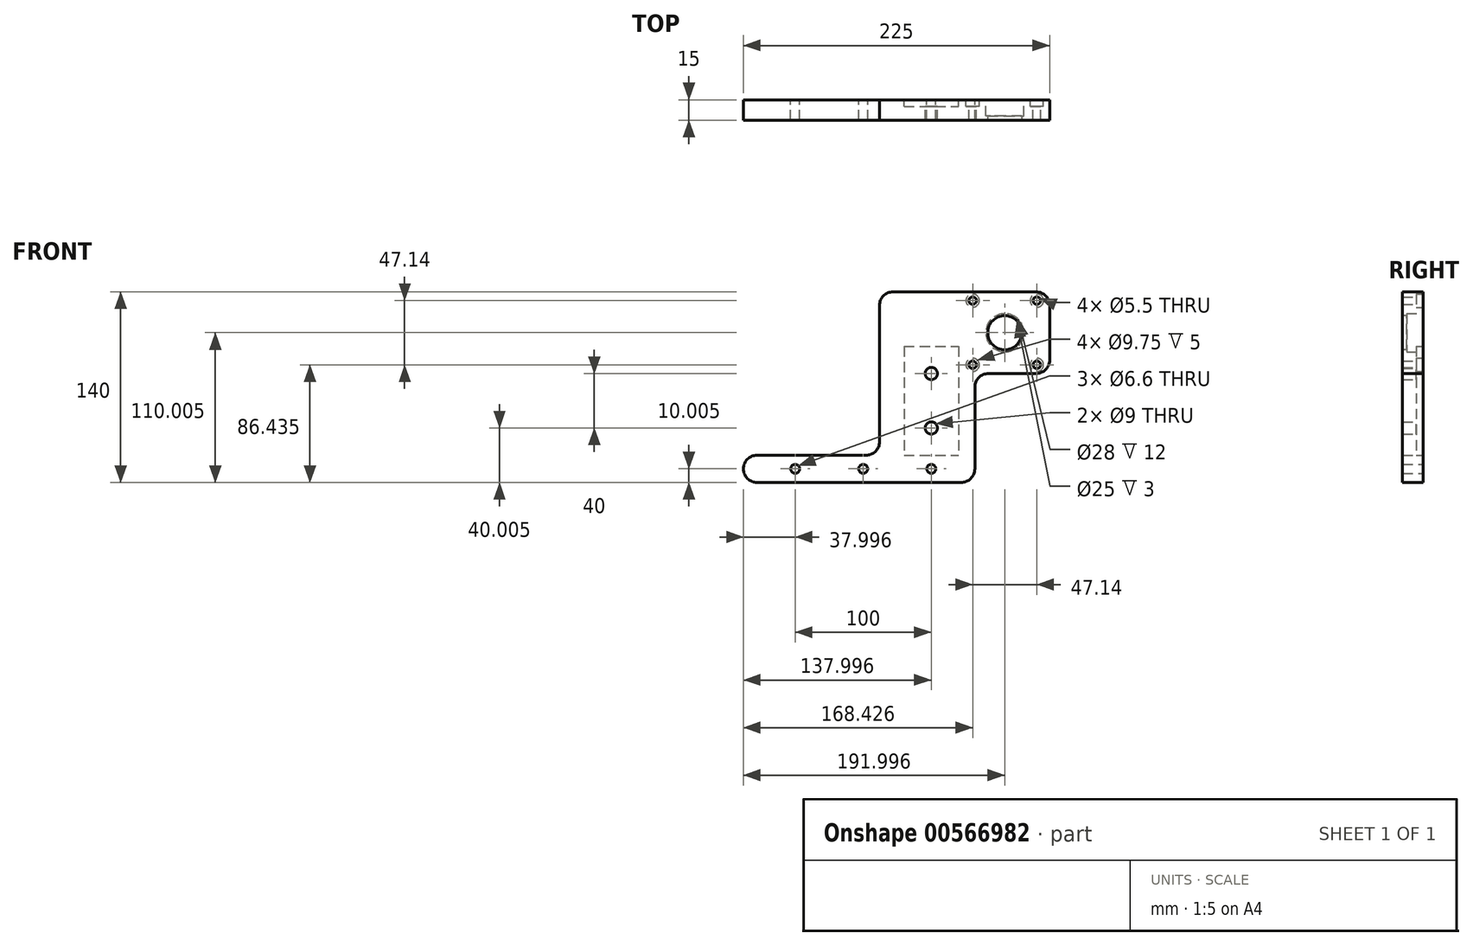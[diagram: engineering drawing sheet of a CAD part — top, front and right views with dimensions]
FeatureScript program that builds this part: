
annotation { "Feature Type Name" : "Feature", "Feature Type Description" : "" }
export const myFeature = defineFeature(function(context is Context, id is Id, definition is map)
    precondition{}
    {
        {
            var Q0;
            Q0=qCreatedBy(makeId("Front.planeOp"),FACE);
            var sketch = newSketch(context, id + "F0", { "sketchPlane" : qUnion([Q0])});
            skLineSegment(sketch, "E0", {"start": v(-57.93, 20.91) * mm, "end": v(62.07, 20.91) * mm});
            skLineSegment(sketch, "E1", {"start": v(62.07, 20.91) * mm, "end": v(62.07, -99.09) * mm});
            skLineSegment(sketch, "E2", {"start": v(62.07, -99.09) * mm, "end": v(162.07, -99.09) * mm});
            skLineSegment(sketch, "E3", {"start": v(162.07, -99.09) * mm, "end": v(162.07, -119.09) * mm});
            skLineSegment(sketch, "E4", {"start": v(162.07, -119.09) * mm, "end": v(-7.93, -119.09) * mm});
            skLineSegment(sketch, "E5", {"start": v(-7.93, -119.09) * mm, "end": v(-7.93, -39.09) * mm});
            skLineSegment(sketch, "E6", {"start": v(-7.93, -39.09) * mm, "end": v(-57.93, -39.09) * mm});
            skLineSegment(sketch, "E7", {"start": v(52.07, 10.91) * mm, "end": v(-47.93, 10.91) * mm, "construction": true});
            skLineSegment(sketch, "E8", {"start": v(-47.93, 10.91) * mm, "end": v(-47.93, -29.09) * mm, "construction": true});
            skLineSegment(sketch, "E9", {"start": v(-47.93, -29.09) * mm, "end": v(4.07, -29.09) * mm, "construction": true});
            skLineSegment(sketch, "E10", {"start": v(4.07, -29.09) * mm, "end": v(4.07, -119.09) * mm, "construction": true});
            skLineSegment(sketch, "E11", {"start": v(4.07, -119.09) * mm, "end": v(162.07, -119.09) * mm, "construction": true});
            skLineSegment(sketch, "E12", {"start": v(162.07, -119.09) * mm, "end": v(162.07, -99.09) * mm, "construction": true});
            skLineSegment(sketch, "E13", {"start": v(162.07, -99.09) * mm, "end": v(52.07, -99.09) * mm, "construction": true});
            skLineSegment(sketch, "E14", {"start": v(52.07, -99.09) * mm, "end": v(52.07, 10.91) * mm, "construction": true});
            skPoint(sketch, "E15", {"position": v(24.07, -109.09) * mm});
            skPoint(sketch, "E16", {"position": v(24.07, -79.09) * mm});
            skPoint(sketch, "E17", {"position": v(24.07, -39.09) * mm});
            skPoint(sketch, "E18", {"position": v(74.07, -109.09) * mm});
            skPoint(sketch, "E19", {"position": v(124.07, -109.09) * mm});
            skPoint(sketch, "E20", {"position": v(-29.93, -9.09) * mm});
            skPoint(sketch, "E21", {"position": v(-53.5, 14.48) * mm});
            skLineSegment(sketch, "E22", {"start": v(-44.33, -9.09) * mm, "end": v(-15.97, -9.09) * mm, "construction": true});
            skLineSegment(sketch, "E23", {"start": v(-29.93, 7.3) * mm, "end": v(-29.93, -21.44) * mm, "construction": true});
            skPoint(sketch, "E24.MirrorP", {"position": v(-53.5, -32.66) * mm});
            skPoint(sketch, "E25.MirrorP", {"position": v(-6.36, 14.48) * mm});
            skPoint(sketch, "E26.MirrorP", {"position": v(-6.36, -32.66) * mm});
            skLineSegment(sketch, "E27", {"start": v(-57.93, 20.91) * mm, "end": v(-62.93, 20.91) * mm});
            skLineSegment(sketch, "E28", {"start": v(-62.93, 20.91) * mm, "end": v(-62.93, -39.09) * mm});
            skLineSegment(sketch, "E29", {"start": v(-62.93, -39.09) * mm, "end": v(-57.93, -39.09) * mm});
            skSolve(sketch);
        }
        {
            var Q0;
            Q0=makeQuery(id+"F0.imprint","IMPRINT",FACE,{"disambiguationData":[TD([[makeQuery(id+"F0.imprint","IMPRINT",EDGE,{"derivedFrom":sQuery(id+"F0.wireOp",EDGE,"E0")}),-1.0]])]});
            extrude(context, id + "F1", {"entities" : qUnion([Q0]), "depth" : 15 * mm});
        }
        {
            var Q0;
            Q0=sQuery(id+"F0.wireOp",VERTEX,"E16");
            var Q1;
            Q1=sQuery(id+"F0.wireOp",VERTEX,"E17");
            var Q2;
            Q2=makeQuery(id+"F1.opExtrude","SWEPT_BODY",BODY,{"disambiguationData":[OSD([sQuery(id+"F0.wireOp",EDGE,"E0"),sQuery(id+"F0.wireOp",EDGE,"E1"),sQuery(id+"F0.wireOp",EDGE,"E2"),sQuery(id+"F0.wireOp",EDGE,"E3"),sQuery(id+"F0.wireOp",EDGE,"E4"),sQuery(id+"F0.wireOp",EDGE,"E5"),sQuery(id+"F0.wireOp",EDGE,"E6"),sQuery(id+"F0.wireOp",EDGE,"cvZF5QLb-uWAo-robz-iAHo-1Gj3ORty2Von")])]});
            hole(context, id + "F2", {"style" : HoleStyle.SIMPLE, "endStyle" : HoleEndStyle.THROUGH, "oppositeDirection" : true, "holeDiameter" : 9 * mm, "locations" : qUnion([Q0, Q1]), "scope" : qUnion([Q2]), "tappedDepth" : 12 * mm, "tapClearance" : 3});
        }
        {
            var Q0;
            Q0=sQuery(id+"F0.wireOp",VERTEX,"E15");
            var Q1;
            Q1=sQuery(id+"F0.wireOp",VERTEX,"E18");
            var Q2;
            Q2=sQuery(id+"F0.wireOp",VERTEX,"E19");
            var Q3;
            Q3=makeQuery(id+"F1.opExtrude","SWEPT_BODY",BODY,{"disambiguationData":[OSD([sQuery(id+"F0.wireOp",EDGE,"E0"),sQuery(id+"F0.wireOp",EDGE,"E1"),sQuery(id+"F0.wireOp",EDGE,"E2"),sQuery(id+"F0.wireOp",EDGE,"E3"),sQuery(id+"F0.wireOp",EDGE,"E4"),sQuery(id+"F0.wireOp",EDGE,"E5"),sQuery(id+"F0.wireOp",EDGE,"E6"),sQuery(id+"F0.wireOp",EDGE,"cvZF5QLb-uWAo-robz-iAHo-1Gj3ORty2Von")])]});
            hole(context, id + "F3", {"style" : HoleStyle.SIMPLE, "endStyle" : HoleEndStyle.THROUGH, "oppositeDirection" : true, "standardTappedOrClearance" : lookupTablePath({ "standard" : "ISO", "fit" : "Normal", "size" : "M6", "type" : "Clearance" }), "standardBlindInLast" : lookupTablePath({ "fit" : "Standard", "standard" : "ISO", "size" : "M6", "type" : "Clearance" }), "holeDiameter" : 6.6 * mm, "locations" : qUnion([Q0, Q1, Q2]), "scope" : qUnion([Q3]), "tappedDepth" : 12 * mm, "tapClearance" : 3});
        }
        {
            var Q0;
            Q0=makeQuery(id+"F1.opExtrude","SWEPT_EDGE",EDGE,{"disambiguationData":[OSD([sQuery(id+"F0.wireOp",EDGE,"E0"),sQuery(id+"F0.wireOp",EDGE,"cvZF5QLb-uWAo-robz-iAHo-1Gj3ORty2Von")])]});
            var Q1;
            Q1=makeQuery(id+"F1.opExtrude","SWEPT_EDGE",EDGE,{"disambiguationData":[OSD([sQuery(id+"F0.wireOp",EDGE,"E1"),sQuery(id+"F0.wireOp",EDGE,"E2")])]});
            var Q2;
            Q2=makeQuery(id+"F1.opExtrude","SWEPT_EDGE",EDGE,{"disambiguationData":[OSD([sQuery(id+"F0.wireOp",EDGE,"E0"),sQuery(id+"F0.wireOp",EDGE,"E1")])]});
            var Q3;
            Q3=makeQuery(id+"F1.opExtrude","SWEPT_EDGE",EDGE,{"disambiguationData":[OSD([sQuery(id+"F0.wireOp",EDGE,"E3"),sQuery(id+"F0.wireOp",EDGE,"E4")])]});
            var Q4;
            Q4=makeQuery(id+"F1.opExtrude","SWEPT_EDGE",EDGE,{"disambiguationData":[OSD([sQuery(id+"F0.wireOp",EDGE,"E2"),sQuery(id+"F0.wireOp",EDGE,"E3")])]});
            var Q5;
            Q5=makeQuery(id+"F1.opExtrude","SWEPT_EDGE",EDGE,{"disambiguationData":[OSD([sQuery(id+"F0.wireOp",EDGE,"E4"),sQuery(id+"F0.wireOp",EDGE,"E5")])]});
            var Q6;
            Q6=makeQuery(id+"F1.opExtrude","SWEPT_EDGE",EDGE,{"disambiguationData":[OSD([sQuery(id+"F0.wireOp",EDGE,"E5"),sQuery(id+"F0.wireOp",EDGE,"E6")])]});
            var Q7;
            Q7=makeQuery(id+"F1.opExtrude","SWEPT_EDGE",EDGE,{"disambiguationData":[OSD([sQuery(id+"F0.wireOp",EDGE,"E6"),sQuery(id+"F0.wireOp",EDGE,"cvZF5QLb-uWAo-robz-iAHo-1Gj3ORty2Von")])]});
            var Q8;
            Q8=makeQuery(id+"F1.opExtrude","SWEPT_EDGE",EDGE,{"disambiguationData":[OSD([sQuery(id+"F0.wireOp",EDGE,"E27"),sQuery(id+"F0.wireOp",EDGE,"E28")])]});
            var Q9;
            Q9=makeQuery(id+"F1.opExtrude","SWEPT_EDGE",EDGE,{"disambiguationData":[OSD([sQuery(id+"F0.wireOp",EDGE,"E28"),sQuery(id+"F0.wireOp",EDGE,"E29")])]});
            fillet(context, id + "F4", {"entities" : qUnion([Q0, Q1, Q2, Q3, Q4, Q5, Q6, Q7, Q8, Q9]), "radius" : 10 * mm, "tangentPropagation" : true, "allowEdgeOverflow" : false});
        }
        {
            var Q0;
            Q0=sQuery(id+"F0.wireOp",VERTEX,"E20");
            var Q1;
            Q1=makeQuery(id+"F1.opExtrude","SWEPT_BODY",BODY,{"disambiguationData":[OSD([sQuery(id+"F0.wireOp",EDGE,"E0"),sQuery(id+"F0.wireOp",EDGE,"E1"),sQuery(id+"F0.wireOp",EDGE,"E2"),sQuery(id+"F0.wireOp",EDGE,"E3"),sQuery(id+"F0.wireOp",EDGE,"E4"),sQuery(id+"F0.wireOp",EDGE,"E5"),sQuery(id+"F0.wireOp",EDGE,"E6"),sQuery(id+"F0.wireOp",EDGE,"cvZF5QLb-uWAo-robz-iAHo-1Gj3ORty2Von")])]});
            hole(context, id + "F5", {"style" : HoleStyle.SIMPLE, "endStyle" : HoleEndStyle.THROUGH, "oppositeDirection" : true, "holeDiameter" : 28 * mm, "locations" : qUnion([Q0]), "scope" : qUnion([Q1]), "tappedDepth" : 12 * mm, "tapClearance" : 3});
        }
        {
            var Q0;
            Q0=sQuery(id+"F0.wireOp",VERTEX,"E21");
            var Q1;
            Q1=sQuery(id+"F0.wireOp",VERTEX,"E25.MirrorP");
            var Q2;
            Q2=sQuery(id+"F0.wireOp",VERTEX,"E26.MirrorP");
            var Q3;
            Q3=sQuery(id+"F0.wireOp",VERTEX,"E24.MirrorP");
            var Q4;
            Q4=makeQuery(id+"F1.opExtrude","SWEPT_BODY",BODY,{"disambiguationData":[OSD([sQuery(id+"F0.wireOp",EDGE,"E0"),sQuery(id+"F0.wireOp",EDGE,"E1"),sQuery(id+"F0.wireOp",EDGE,"E2"),sQuery(id+"F0.wireOp",EDGE,"E3"),sQuery(id+"F0.wireOp",EDGE,"E4"),sQuery(id+"F0.wireOp",EDGE,"E5"),sQuery(id+"F0.wireOp",EDGE,"E6"),sQuery(id+"F0.wireOp",EDGE,"cvZF5QLb-uWAo-robz-iAHo-1Gj3ORty2Von")])]});
            hole(context, id + "F6", {"style" : HoleStyle.C_BORE, "endStyle" : HoleEndStyle.THROUGH, "oppositeDirection" : true, "standardTappedOrClearance" : lookupTablePath({ "standard" : "ISO", "fit" : "Normal", "size" : "M5", "type" : "Clearance" }), "standardBlindInLast" : lookupTablePath({ "fit" : "Standard", "standard" : "ISO", "size" : "M5", "type" : "Clearance" }), "holeDiameter" : 5.5 * mm, "cBoreDiameter" : 9.75 * mm, "cBoreDepth" : 5 * mm, "locations" : qUnion([Q0, Q1, Q2, Q3]), "scope" : qUnion([Q4]), "tappedDepth" : 12 * mm, "tapClearance" : 3});
        }
        {
            var Q0;
            Q0=makeQuery(id+"F0.imprint","IMPRINT",FACE,{"disambiguationData":[TD([[makeQuery(id+"F0.imprint","IMPRINT",EDGE,{"derivedFrom":sQuery(id+"F0.wireOp",EDGE,"E0")}),-1.0]])]});
            var sketch = newSketch(context, id + "F7", { "sketchPlane" : qUnion([Q0])});
            skLineSegment(sketch, "E30.bottom", {"start": v(44.07, -19.09) * mm, "end": v(4.07, -19.09) * mm});
            skLineSegment(sketch, "E30.top", {"start": v(44.07, -99.09) * mm, "end": v(4.07, -99.09) * mm});
            skLineSegment(sketch, "E30.left", {"start": v(44.07, -19.09) * mm, "end": v(44.07, -99.09) * mm});
            skLineSegment(sketch, "E30.right", {"start": v(4.07, -19.09) * mm, "end": v(4.07, -99.09) * mm});
            skSolve(sketch);
        }
        {
            var Q0;
            Q0=qSketchRegion(id+"F7",true);
            extrude(context, id + "F8", {"entities" : qUnion([Q0]), "operationType" : NewBodyOperationType.REMOVE, "depth" : 5 * mm});
        }
        {
            var Q0;
            Q0=qCreatedBy(makeId("Right.planeOp"),FACE);
            cPlane(context, id + "F9", {"entities" : qUnion([Q0]), "cplaneType" : CPlaneType.OFFSET, "offset" : 100 * mm, "oppositeDirection" : true, "width" : 150 * mm, "height" : 150 * mm});
        }
        {
            var Q0;
            Q0=makeQuery(id+"F1.opExtrude","SWEPT_BODY",BODY,{"disambiguationData":[OSD([sQuery(id+"F0.wireOp",EDGE,"E0"),sQuery(id+"F0.wireOp",EDGE,"E1"),sQuery(id+"F0.wireOp",EDGE,"E2"),sQuery(id+"F0.wireOp",EDGE,"E3"),sQuery(id+"F0.wireOp",EDGE,"E4"),sQuery(id+"F0.wireOp",EDGE,"E5"),sQuery(id+"F0.wireOp",EDGE,"E6"),sQuery(id+"F0.wireOp",EDGE,"E27"),sQuery(id+"F0.wireOp",EDGE,"E28"),sQuery(id+"F0.wireOp",EDGE,"E29")])]});
            var Q1;
            Q1=qCreatedBy(id+"F9.planeOp",FACE);
            mirror(context, id + "F10", {"entities" : qUnion([Q0]), "mirrorPlane" : qUnion([Q1])});
        }
        {
            var Q0;
            Q0=makeQuery(id+"F10.opPattern","COPY",FACE,{"derivedFrom":makeQuery(id+"F1.opExtrude","CAP_FACE",FACE,{"disambiguationData":[OSD([sQuery(id+"F0.wireOp",EDGE,"E0"),sQuery(id+"F0.wireOp",EDGE,"E1"),sQuery(id+"F0.wireOp",EDGE,"E2"),sQuery(id+"F0.wireOp",EDGE,"E3"),sQuery(id+"F0.wireOp",EDGE,"E4"),sQuery(id+"F0.wireOp",EDGE,"E5"),sQuery(id+"F0.wireOp",EDGE,"E6"),sQuery(id+"F0.wireOp",EDGE,"E27"),sQuery(id+"F0.wireOp",EDGE,"E28"),sQuery(id+"F0.wireOp",EDGE,"E29")])],"isStart":false}),"instanceName":"1"});
            var sketch = newSketch(context, id + "F11", { "sketchPlane" : qUnion([Q0])});
            skCircle(sketch, "E31", {"center": v(-170.07, -9.09) * mm, "radius": 12.5 * mm});
            skCircle(sketch, "E32", {"center": v(-170.07, -9.09) * mm, "radius": 14 * mm});
            skSolve(sketch);
        }
        {
            var Q0;
            Q0=makeQuery(id+"F11.imprint","IMPRINT",FACE,{"disambiguationData":[TD([[makeQuery(id+"F11.imprint","IMPRINT",EDGE,{"derivedFrom":sQuery(id+"F11.wireOp",EDGE,"E31")}),-1.0]])]});
            extrude(context, id + "F12", {"entities" : qUnion([Q0]), "operationType" : NewBodyOperationType.ADD, "oppositeDirection" : true, "depth" : 3 * mm});
        }
        {
            var Q0;
            Q0=makeQuery(id+"F1.opExtrude","SWEPT_BODY",BODY,{"disambiguationData":[OSD([sQuery(id+"F0.wireOp",EDGE,"E0"),sQuery(id+"F0.wireOp",EDGE,"E1"),sQuery(id+"F0.wireOp",EDGE,"E2"),sQuery(id+"F0.wireOp",EDGE,"E3"),sQuery(id+"F0.wireOp",EDGE,"E4"),sQuery(id+"F0.wireOp",EDGE,"E5"),sQuery(id+"F0.wireOp",EDGE,"E6"),sQuery(id+"F0.wireOp",EDGE,"E27"),sQuery(id+"F0.wireOp",EDGE,"E28"),sQuery(id+"F0.wireOp",EDGE,"E29")])]});
            deleteBodies(context, id + "F13", {"entities" : qUnion([Q0])});
        }
    });
